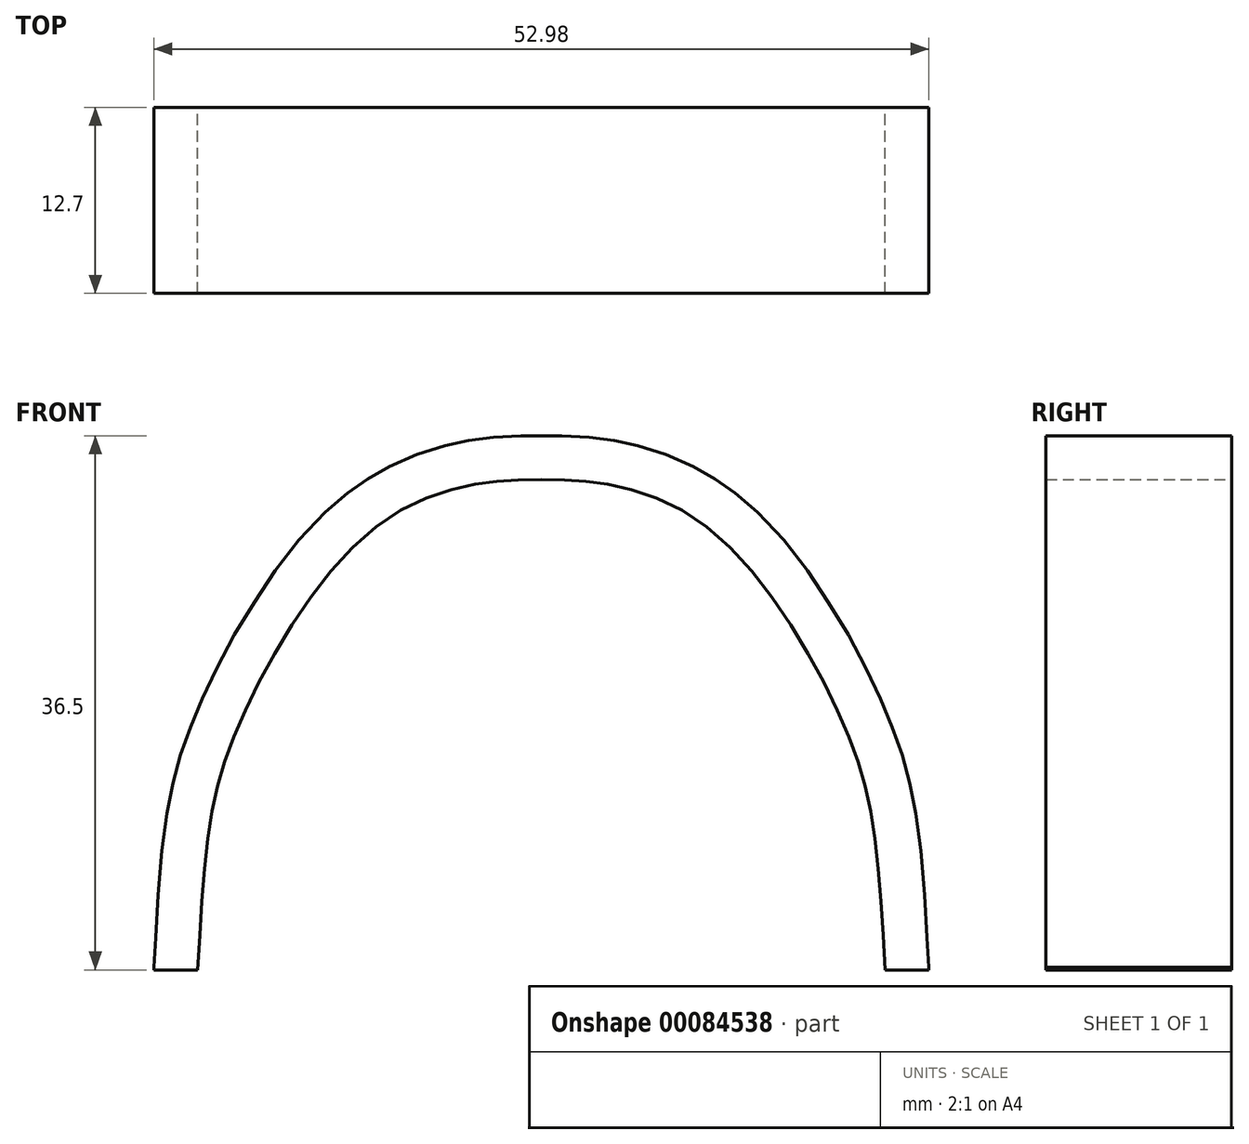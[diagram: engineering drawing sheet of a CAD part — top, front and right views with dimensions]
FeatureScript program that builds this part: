
annotation { "Feature Type Name" : "Feature", "Feature Type Description" : "" }
export const myFeature = defineFeature(function(context is Context, id is Id, definition is map)
    precondition{}
    {
        {
            var Q0;
            Q0=qCreatedBy(makeId("Front.planeOp"),FACE);
            var sketch = newSketch(context, id + "F0", { "sketchPlane" : qUnion([Q0]) });
            skPoint(sketch, "E0", {"position": v(0.8, 9.7) * mm});
            skPoint(sketch, "E1", {"position": v(2.4, 15.7) * mm});
            skPoint(sketch, "E2", {"position": v(6.6, 23.8) * mm});
            skPoint(sketch, "E3", {"position": v(12.9, 30.8) * mm});
            skPoint(sketch, "E4", {"position": v(19, 33.2) * mm});
            skPoint(sketch, "E5", {"position": v(23.5, 33.5) * mm});
            skFitSpline(sketch, "E6", {"points": [v(0, 0) * mm, v(0.8, 9.7) * mm, v(2.4, 15.7) * mm, v(6.6, 23.8) * mm, v(12.9, 30.8) * mm, v(19, 33.2) * mm, v(23.5, 33.5) * mm], "startDerivative": vector(3.54, 54.69) * mm, "endDerivative": vector(39.27, 0) * mm});
            skLineSegment(sketch, "E7", {"start": v(23.5, 33.5) * mm, "end": v(23.5, 0) * mm, "construction": true});
            skFitSpline(sketch, "E8.MirrorCS", {"points": [v(47, 0) * mm, v(46.2, 9.7) * mm, v(44.6, 15.7) * mm, v(40.4, 23.8) * mm, v(34.1, 30.8) * mm, v(28, 33.2) * mm, v(23.5, 33.5) * mm], "startDerivative": vector(-3.54, 54.69) * mm, "endDerivative": vector(-39.27, 0) * mm});
            skFitSpline(sketch, "E9.0", {"points": [v(50, 0.2) * mm, v(49.92, 1.32) * mm, v(49.78, 3.6) * mm, v(49.55, 6.93) * mm, v(49.27, 9.53) * mm, v(48.96, 11.45) * mm, v(48.67, 12.83) * mm, v(48.31, 14.17) * mm, v(47.88, 15.5) * mm, v(47.38, 16.85) * mm, v(46.8, 18.24) * mm, v(46.14, 19.68) * mm, v(45.16, 21.65) * mm, v(44.04, 23.66) * mm, v(42.8, 25.64) * mm, v(41.47, 27.6) * mm, v(40, 29.48) * mm, v(38.35, 31.2) * mm, v(37.24, 32.2) * mm, v(36.3, 32.92) * mm, v(35.57, 33.44) * mm, v(34.82, 33.9) * mm, v(33.81, 34.45) * mm, v(32.55, 35.02) * mm, v(31.08, 35.55) * mm, v(29.9, 35.87) * mm, v(29, 36.07) * mm, v(28.12, 36.23) * mm, v(27.08, 36.37) * mm, v(25.89, 36.46) * mm, v(24.72, 36.5) * mm, v(23.92, 36.5) * mm, v(23.5, 36.5) * mm]});
            skFitSpline(sketch, "E9.1", {"points": [v(-3, 0.2) * mm, v(-2.92, 1.32) * mm, v(-2.78, 3.6) * mm, v(-2.55, 6.93) * mm, v(-2.27, 9.53) * mm, v(-1.96, 11.45) * mm, v(-1.67, 12.83) * mm, v(-1.31, 14.17) * mm, v(-0.88, 15.5) * mm, v(-0.38, 16.85) * mm, v(0.2, 18.24) * mm, v(0.86, 19.68) * mm, v(1.84, 21.65) * mm, v(2.96, 23.66) * mm, v(4.2, 25.64) * mm, v(5.53, 27.6) * mm, v(7, 29.48) * mm, v(8.65, 31.2) * mm, v(9.76, 32.2) * mm, v(10.7, 32.92) * mm, v(11.43, 33.44) * mm, v(12.18, 33.9) * mm, v(13.19, 34.45) * mm, v(14.45, 35.02) * mm, v(15.92, 35.55) * mm, v(17.1, 35.87) * mm, v(18, 36.07) * mm, v(18.88, 36.23) * mm, v(19.92, 36.37) * mm, v(21.11, 36.46) * mm, v(22.28, 36.5) * mm, v(23.08, 36.5) * mm, v(23.5, 36.5) * mm]});
            skLineSegment(sketch, "E10", {"start": v(-3, 0.2) * mm, "end": v(-3, 0) * mm});
            skLineSegment(sketch, "E11.MirrorCS", {"start": v(50, 0.2) * mm, "end": v(50, 0) * mm});
            skLineSegment(sketch, "E12", {"start": v(-3, 0) * mm, "end": v(0, 0) * mm});
            skLineSegment(sketch, "E13.MirrorCS", {"start": v(50, 0) * mm, "end": v(47, 0) * mm});
            skSolve(sketch);
        }
        {
            var Q0;
            Q0 = qSketchRegion(id + "F0", true);
            extrude(context, id + "F1", {"entities" : qUnion([Q0]), "depth" : 12.7 * mm});
        }
    });
